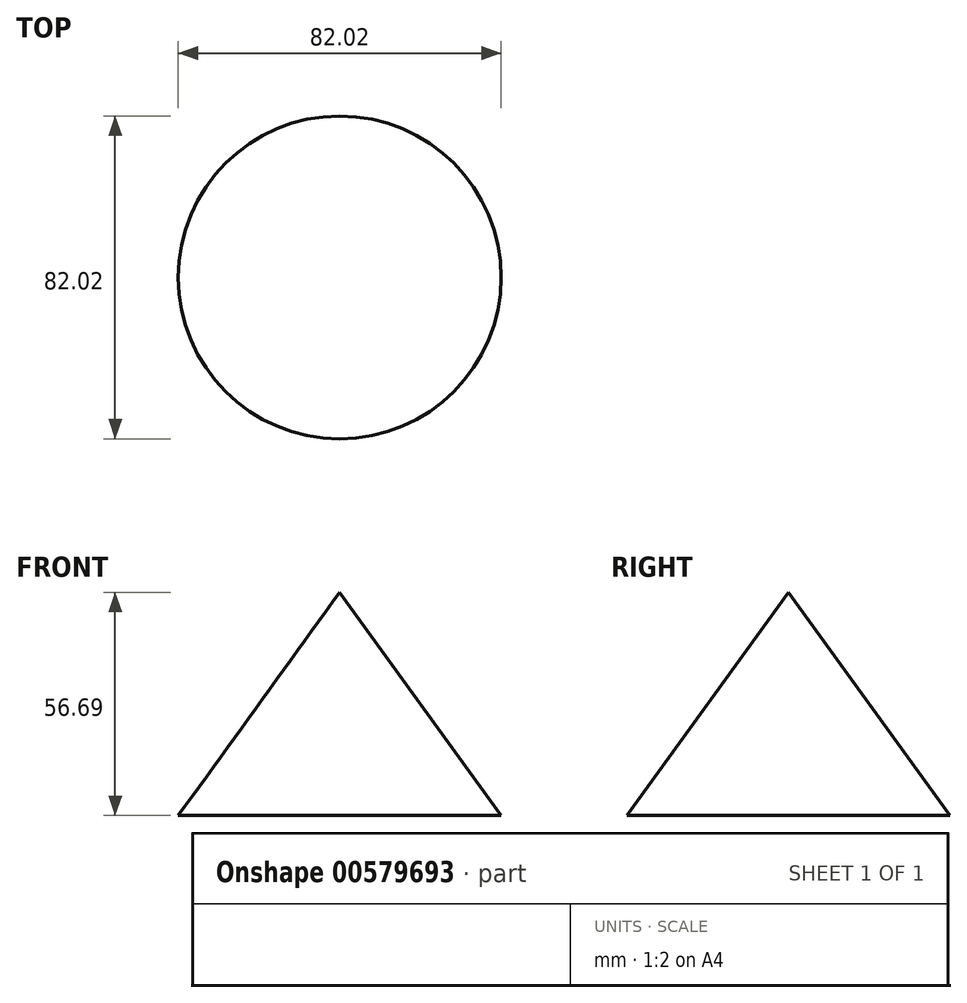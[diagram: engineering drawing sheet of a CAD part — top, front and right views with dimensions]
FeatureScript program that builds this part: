
annotation { "Feature Type Name" : "Feature", "Feature Type Description" : "" }
export const myFeature = defineFeature(function(context is Context, id is Id, definition is map)
    precondition{}
    {
        {
            var Q0;
            Q0=qCreatedBy(makeId("Front.planeOp"),FACE);
            var sketch = newSketch(context, id + "F0", { "sketchPlane" : qUnion([Q0])});
            skLineSegment(sketch, "E0", {"start": v(0, 0) * mm, "end": v(0, 56.7) * mm});
            skLineSegment(sketch, "E1", {"start": v(0, 56.7) * mm, "end": v(41.01, 0) * mm});
            skLineSegment(sketch, "E2", {"start": v(41.01, 0) * mm, "end": v(0, 0) * mm});
            skSolve(sketch);
        }
        {
            var Q0;
            Q0=makeQuery(id+"F0.imprint","IMPRINT",FACE,{"disambiguationData":[TD([[makeQuery(id+"F0.imprint","IMPRINT",EDGE,{"derivedFrom":sQuery(id+"F0.wireOp",EDGE,"E0")}),-1.0]])]});
            var Q1;
            Q1=sQuery(id+"F0.wireOp",EDGE,"E0");
            revolve(context, id + "F1", {"entities" : qUnion([Q0]), "axis" : qUnion([Q1]), "revolveType" : RevolveType.FULL});
        }
    });
